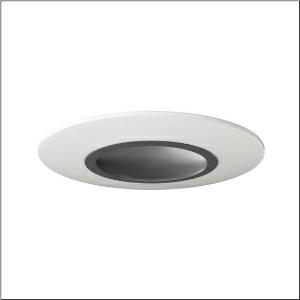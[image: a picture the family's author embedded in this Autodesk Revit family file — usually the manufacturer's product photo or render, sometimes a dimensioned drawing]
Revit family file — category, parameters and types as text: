
# Revit family: rondel_21_0md5307l1840
name_source: partatom
category: Lighting Fixtures
units: mm (PartAtom-declared; Revit-internal decimal feet)

## family parameters
Cut with Voids When Loaded = No
Host = Face
Light Source = No
Part Type = Normal
Room Calculation Point = No
Round Connector Dimension = Use Diameter
Shared = No

## types (1)
- Rondel 21 (1 x LED 4000K / CRI = 80 (unbekannt), 1800 lm, 4000K)
    Apparent Load = 18 VA
    CIE Flux Codes = 43 74 92 91 100
    Color Rendering = 80
    Color Temperature = 4000K
    Default Elevation = 1800 mm  [stored 5.90551 ft]
    Description = Rondel 21, wall and ceiling luminaire, of PC, opal, light emission: direct distribution, installation type: surface-mounted, LED, rated luminous flux: 1.800lm, luminous efficacy: 100lm/W, light colour: 840, colour temperature: 4000K, control gear: ECG, with terminal, 2-pole, mains connection: 220..240V, AC, 50/60Hz, rated input power: 18W, housing, round, of sheet steel, powder-coated, white, diameter: 380mm, height: 28mm, cover, of PC, graphite (RAL 7037), protection rating (complete): IP40, insulation class (complete): insulation class II (safety insulation), certification: CE, impact resistance: IK03, permissible operating ambient temperature: -20..+40°C, permissible storage temperature: -20..+80°C, packaging unit: 1 piece
    Height = 28 mm
    Lamp = 1 x LED 4000K / CRI >= 80 (unbekannt)
    Lamp Light Flux = 1800 lm
    Lamp count = 1
    Length = 380 mm
    Luminous efficacy = 100 lm/W
    Manufacturer = Siteco
    ModVariant = No
    Model = 0MD5307L1840
    Mounting Place = Ceiling
    Mounting Type = Surface mounted
    Number of Poles = 1
    OnlyDefault = Yes
    Power Factor = 1
    Product Name = Rondel 21
    Product group = wall and ceiling luminaire
    ProductGroupID = 302
    Protection Class = Protection class II
    Protection Degree = IP 40
    RLX_Detail_Level = 1
    RLX_Emergency_Light_Flux = 0 lm
    RLX_Emergency_Type = 0
    RLX_Emergency_Type_DB = No
    RlxData = <blob elided: 61705 chars, md5=425c8acb>
    Socket = socket
    Standby Power = 0 W
    System Light Flux = 1800 lm
    System Power = 18 W
    Type Comments = Product without accessories
    Type Image = l_1005688.jpg
    URL = http://relux.com
    VarID = ---
    Voltage = 0 V
    Weight = 0.00 kg
    Width = 0 mm  [stored 0 ft]

note: [stored X ft] marks values corroborated as IEEE doubles in the binary element streams (Revit-internal decimal feet)

## geometry (parser evidence)
native form markers: Blend x4, Sweep x13
no freeform markers — native parametric forms only
